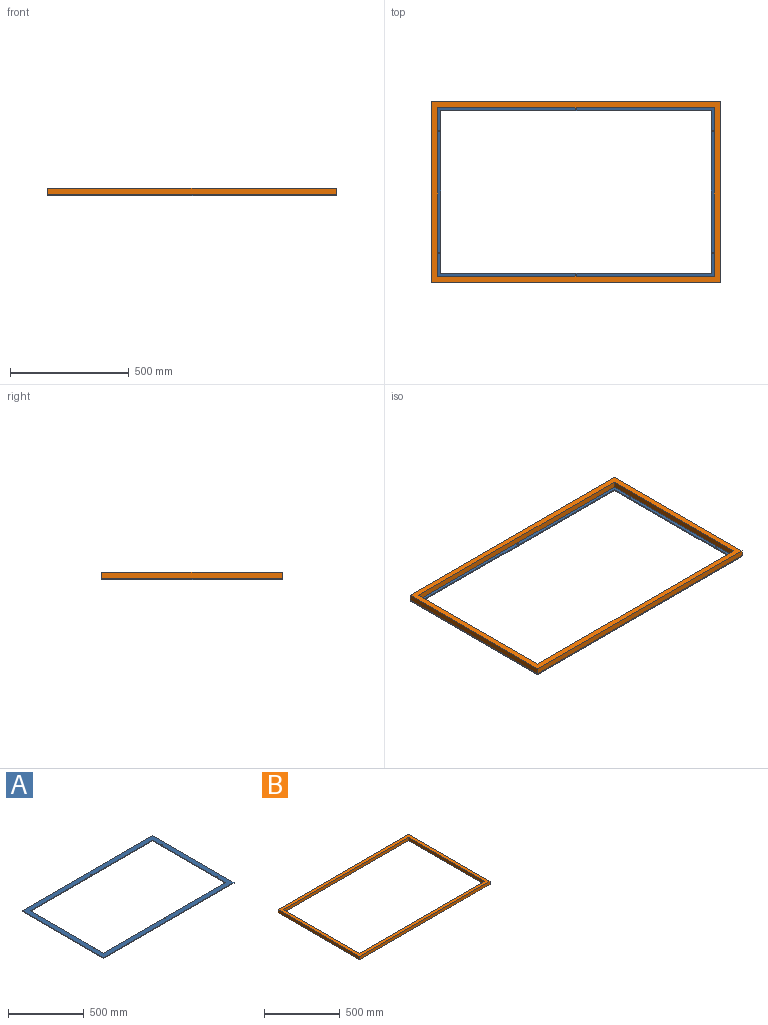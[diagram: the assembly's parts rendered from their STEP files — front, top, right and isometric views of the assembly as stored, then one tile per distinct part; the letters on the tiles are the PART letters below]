
ASSEMBLY  parts=2 mates=1
PART A: 16 faces, bbox 1219.2x762x4.8 mm
  f0: plane 1219.2x4.76mm, normal (0,1,0), area 5806.4mm2, adj f1,f13,f14,f15
  f1: plane 762x4.76mm, normal (-1,0,0), area 3629mm2, adj f0,f2,f14,f15
  f2: plane 1219.2x4.76mm, normal (0,-1,0), area 5806.4mm2, adj f1,f13,f14,f15
  f3: plane 685.8x4.76mm, normal (1,0,0), area 3266.1mm2, adj f4,f6,f14,f15
  f4: plane 1143x4.76mm, normal (0,-1,0), area 5443.5mm2, adj f3,f5,f14,f15
  f5: plane 685.8x4.76mm, normal (-1,0,0), area 3266.1mm2, adj f4,f6,f14,f15
  f6: plane 1143x4.76mm, normal (0,1,0), area 5443.5mm2, adj f3,f5,f14,f15
  f7: cylinder r=3.17mm len=6.35mm, axis (0,0,-1), area 95mm2, adj f14,f15
  f8: cylinder r=3.17mm len=6.35mm, axis (0,0,-1), area 95mm2, adj f14,f15
  f9: cylinder r=3.17mm len=6.35mm, axis (0,0,-1), area 95mm2, adj f14,f15
  f10: cylinder r=3.17mm len=6.35mm, axis (0,0,-1), area 95mm2, adj f14,f15
  f11: cylinder r=3.17mm len=6.35mm, axis (0,0,-1), area 95mm2, adj f14,f15
  f12: cylinder r=3.17mm len=6.35mm, axis (0,0,-1), area 95mm2, adj f14,f15
  f13: plane 762x4.76mm, normal (1,0,0), area 3629mm2, adj f0,f2,f14,f15
  f14: plane 1219.2x762mm, normal (0,0,1), area 144971mm2, adj f0,f1,f2,f3,f4,f5,f6,f7
  f15: plane 1219.2x762mm, normal (0,0,-1), area 144971mm2, adj f0,f1,f2,f3,f4,f5,f6,f7
PART B: 10 faces, bbox 1219.2x762x25.4 mm
  f0: plane 1219.2x25.4mm, normal (0,-1,0), area 30967.7mm2, adj f1,f7,f8,f9
  f1: plane 762x25.4mm, normal (1,0,0), area 19354.8mm2, adj f0,f2,f8,f9
  f2: plane 1219.2x25.4mm, normal (0,1,0), area 30967.7mm2, adj f1,f7,f8,f9
  f3: plane 711.2x25.4mm, normal (1,0,0), area 18064.5mm2, adj f4,f6,f8,f9
  f4: plane 1168.4x25.4mm, normal (0,-1,0), area 29677.4mm2, adj f3,f5,f8,f9
  f5: plane 711.2x25.4mm, normal (-1,0,0), area 18064.5mm2, adj f4,f6,f8,f9
  f6: plane 1168.4x25.4mm, normal (0,1,0), area 29677.4mm2, adj f3,f5,f8,f9
  f7: plane 762x25.4mm, normal (-1,0,0), area 19354.8mm2, adj f0,f2,f8,f9
  f8: plane 1219.2x762mm, normal (0,0,1), area 98064.3mm2, adj f0,f1,f2,f3,f4,f5,f6,f7
  f9: plane 1219.2x762mm, normal (0,0,-1), area 98064.3mm2, adj f0,f1,f2,f3,f4,f5,f6,f7
PLACE A t=(5.05,86.4,-18.56)mm
PLACE B t=(74.01,35.12,-13.8)mm
MATE fastened A.f14 <-> B.f9  axis (0,0,1) through (-604.55,-294.6,-13.8)mm
